# Revit family: ACO TD2-902 In-line pit
name_source: partatom
category: Plumbing Fixtures
units: mm (PartAtom-declared; Revit-internal decimal feet)

## family parameters
Always vertical = Yes
Cut with Voids When Loaded = No
OmniClass Number = 23.70.50.24
OmniClass Title = Rainwater Removal
Part Type = Normal
Room Calculation Point = No
Round Connector Dimension = Use Diameter
Shared = No
Work Plane-Based = No

## types (1)
- TD2-902 In-line pit
    Description = ACO TD200 In-line pit
    IfcDescription = ACO TD200 In-line pit
    IfcExportAs = IfcWasteTerminalType
    IfcExportType = USERDEFINED
    Manufacturer = ACO
    Model = TD200 In-line pit
    Telephone = 1300 765 226
    URL = https://www.acoinfrastructure.com.au
    content_date_changed_C_ANZRS = 20-07-2021
    content_version_C_ANZRS = 1.0
    info_commercial_C_ANZRS = https://www.acoinfrastructure.com.au
    info_technical_C_ANZRS = https://www.acoinfrastructure.com.au
    installation_manual = https://www.acoinfrastructure.com.au
    instructions_for_use = https://www.acoinfrastructure.com.au
    intended_use_C_ANZRS = Drainage systems
    lookup_table_name = Neutral channel_TD200
    material_01_C_ANZRS = Polymer Concrete
    material_02_C_ANZRS = PE, Black
    material_C_ANZRS = Iron, cast
    region_index = 1
    type_index = 1

## geometry (parser evidence)
native form markers: Sweep x12
no freeform markers — native parametric forms only
